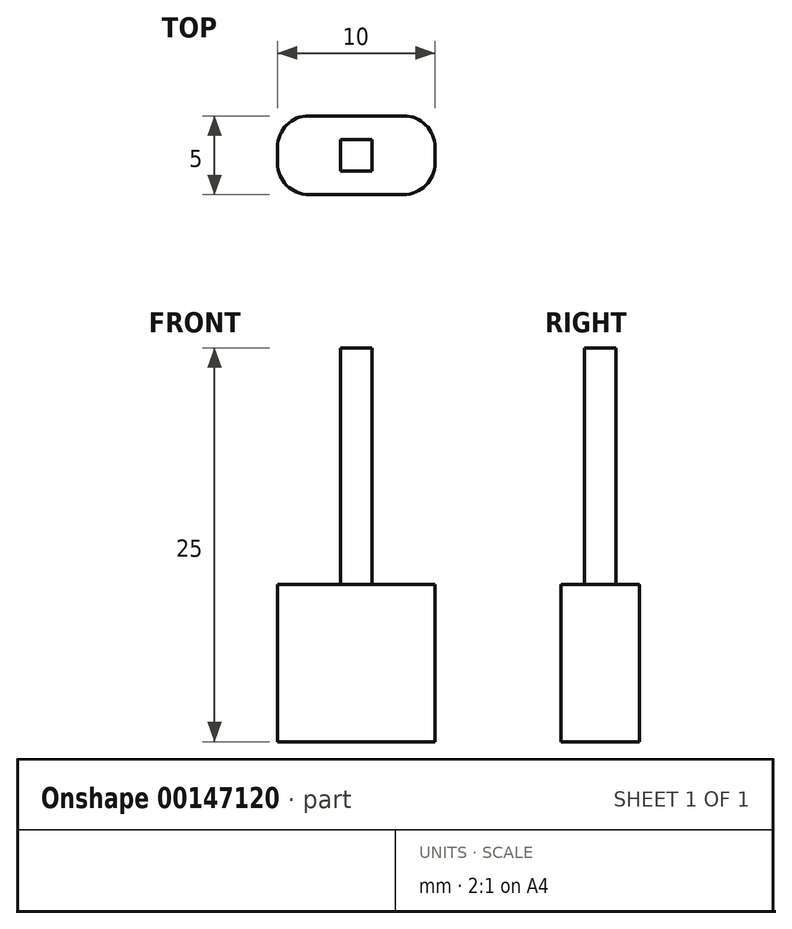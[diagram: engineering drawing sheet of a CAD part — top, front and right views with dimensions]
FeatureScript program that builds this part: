
annotation { "Feature Type Name" : "Feature", "Feature Type Description" : "" }
export const myFeature = defineFeature(function(context is Context, id is Id, definition is map)
    precondition{}
    {
        {
            var Q0;
            Q0=qCreatedBy(makeId("Top.planeOp"),FACE);
            var sketch = newSketch(context, id + "F0", { "sketchPlane" : qUnion([Q0])});
            skLineSegment(sketch, "E0.bottom", {"start": v(5, 2.5) * mm, "end": v(-5, 2.5) * mm});
            skLineSegment(sketch, "E0.top", {"start": v(5, -2.5) * mm, "end": v(-5, -2.5) * mm});
            skLineSegment(sketch, "E0.left", {"start": v(5, 2.5) * mm, "end": v(5, -2.5) * mm});
            skLineSegment(sketch, "E0.right", {"start": v(-5, 2.5) * mm, "end": v(-5, -2.5) * mm});
            skPoint(sketch, "E0.middle", {"position": v(0, 0) * mm});
            skLineSegment(sketch, "E1.bottom", {"start": v(1, 1) * mm, "end": v(-1, 1) * mm});
            skLineSegment(sketch, "E1.top", {"start": v(1, -1) * mm, "end": v(-1, -1) * mm});
            skLineSegment(sketch, "E1.left", {"start": v(1, 1) * mm, "end": v(1, -1) * mm});
            skLineSegment(sketch, "E1.right", {"start": v(-1, 1) * mm, "end": v(-1, -1) * mm});
            skSolve(sketch);
        }
        {
            var Q0;
            Q0 = qSketchRegion(id + "F0", true);
            var Q1;
            Q1=makeQuery(id+"F0.imprint","IMPRINT",FACE,{"disambiguationData":[TD([[makeQuery(id+"F0.imprint","IMPRINT",EDGE,{"derivedFrom":sQuery(id+"F0.wireOp",EDGE,"E1.bottom")}),1.0]])]});
            extrude(context, id + "F1", {"entities" : qUnion([Q0, Q1]), "oppositeDirection" : true, "depth" : 10 * mm});
        }
        {
            var Q0;
            Q0=makeQuery(id+"F0.imprint","IMPRINT",FACE,{"disambiguationData":[TD([[makeQuery(id+"F0.imprint","IMPRINT",EDGE,{"derivedFrom":sQuery(id+"F0.wireOp",EDGE,"E1.bottom")}),1.0]])]});
            extrude(context, id + "F2", {"entities" : qUnion([Q0]), "operationType" : NewBodyOperationType.ADD, "depth" : 15 * mm});
        }
        {
            var Q0;
            Q0=makeQuery(id+"F1.opExtrude","SWEPT_EDGE",EDGE,{"disambiguationData":[OSD([sQuery(id+"F0.wireOp",EDGE,"E0.top"),sQuery(id+"F0.wireOp",EDGE,"E0.left")])]});
            var Q1;
            Q1=makeQuery(id+"F1.opExtrude","SWEPT_EDGE",EDGE,{"disambiguationData":[OSD([sQuery(id+"F0.wireOp",EDGE,"E0.top"),sQuery(id+"F0.wireOp",EDGE,"E0.right")])]});
            var Q2;
            Q2=makeQuery(id+"F1.opExtrude","SWEPT_EDGE",EDGE,{"disambiguationData":[OSD([sQuery(id+"F0.wireOp",EDGE,"E0.bottom"),sQuery(id+"F0.wireOp",EDGE,"E0.right")])]});
            var Q3;
            Q3=makeQuery(id+"F1.opExtrude","SWEPT_EDGE",EDGE,{"disambiguationData":[OSD([sQuery(id+"F0.wireOp",EDGE,"E0.bottom"),sQuery(id+"F0.wireOp",EDGE,"E0.left")])]});
            fillet(context, id + "F3", {"entities" : qUnion([Q0, Q1, Q2, Q3]), "radius" : 2 * mm, "tangentPropagation" : true, "allowEdgeOverflow" : false});
        }
    });
